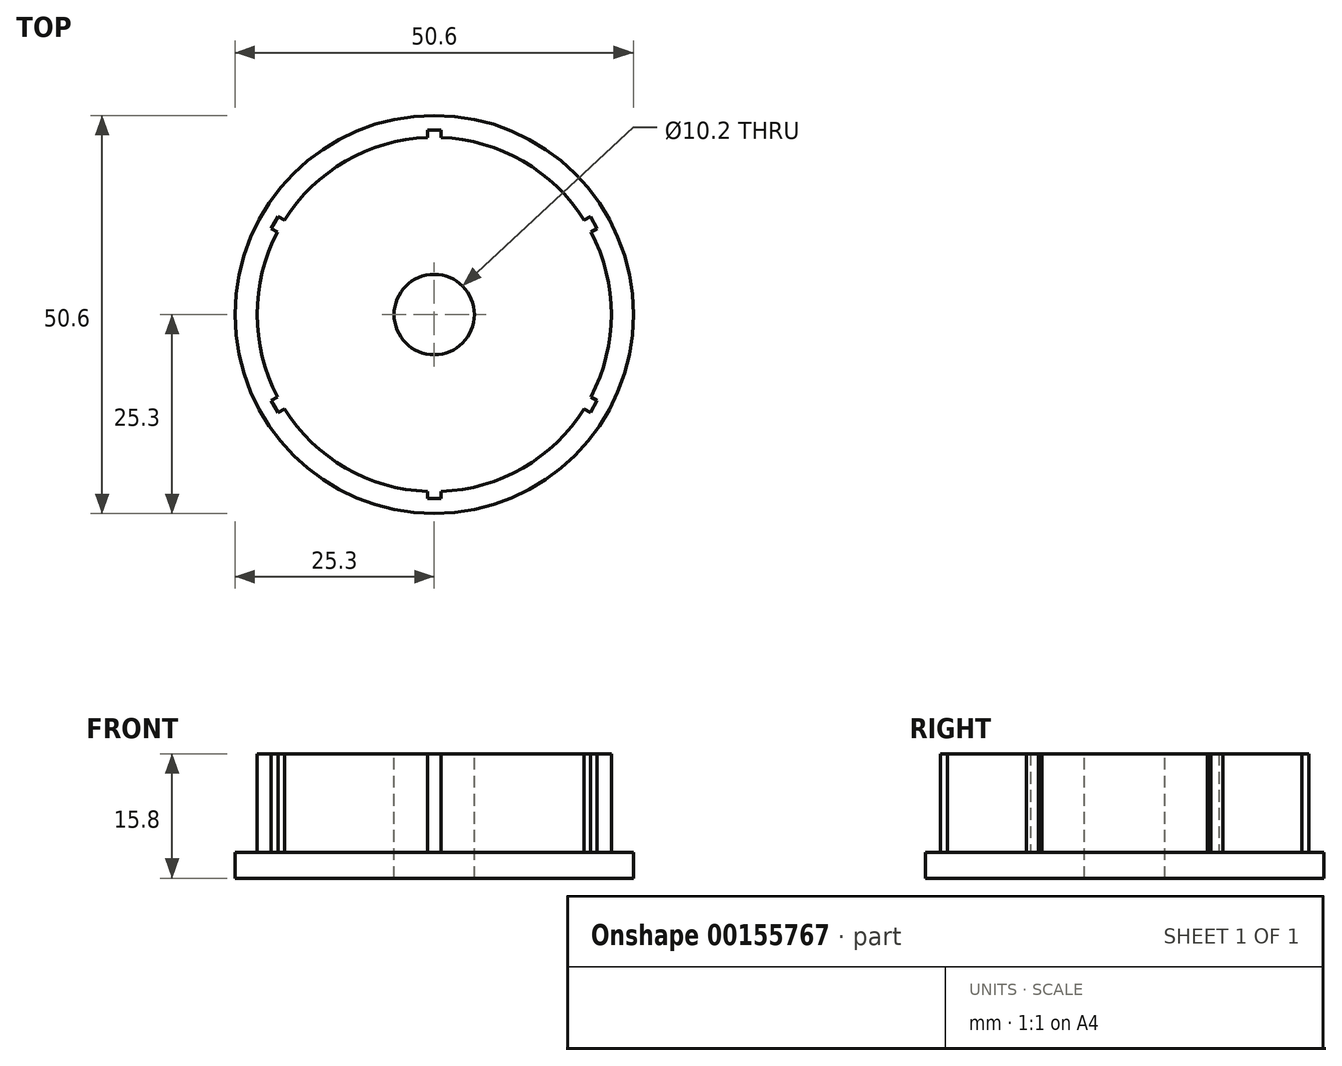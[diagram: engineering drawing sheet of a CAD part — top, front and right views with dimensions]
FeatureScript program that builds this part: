
annotation { "Feature Type Name" : "Feature", "Feature Type Description" : "" }
export const myFeature = defineFeature(function(context is Context, id is Id, definition is map)
    precondition{}
    {
        {
            var Q0;
            Q0=qCreatedBy(makeId("Top.planeOp"),FACE);
            var sketch = newSketch(context, id + "F0", { "sketchPlane" : qUnion([Q0])});
            skCircle(sketch, "E0", {"center": v(0, 0) * mm, "radius": 25.3 * mm});
            skSolve(sketch);
        }
        {
            var Q0;
            Q0 = qSketchRegion(id + "F0", true);
            extrude(context, id + "F1", {"entities" : qUnion([Q0]), "depth" : 3.3 * mm, "offsetDistance" : 25 * mm});
        }
        {
            var Q0;
            Q0=makeQuery(id+"F1.opExtrude","CAP_FACE",FACE,{"disambiguationData":[OSD([sQuery(id+"F0.wireOp",EDGE,"E0")])],"isStart":false});
            var sketch = newSketch(context, id + "F2", { "sketchPlane" : qUnion([Q0])});
            skCircle(sketch, "E1", {"center": v(0, 0) * mm, "radius": 22.5 * mm});
            skLineSegment(sketch, "E2", {"start": v(-0.87, 22.48) * mm, "end": v(-0.88, 23.4) * mm});
            skLineSegment(sketch, "E3.MirrorCS", {"start": v(0.88, 22.48) * mm, "end": v(0.88, 23.4) * mm});
            skLineSegment(sketch, "E4", {"start": v(-0.88, 23.4) * mm, "end": v(0.88, 23.4) * mm});
            skLineSegment(sketch, "E5.1.0", {"start": v(-19.9, 10.48) * mm, "end": v(-20.7, 10.94) * mm});
            skLineSegment(sketch, "E5.1.1", {"start": v(-20.7, 10.94) * mm, "end": v(-19.83, 12.46) * mm});
            skLineSegment(sketch, "E5.1.2", {"start": v(-19.03, 12) * mm, "end": v(-19.83, 12.46) * mm});
            skLineSegment(sketch, "E5.2.0", {"start": v(-19.03, -12) * mm, "end": v(-19.83, -12.46) * mm});
            skLineSegment(sketch, "E5.2.1", {"start": v(-19.83, -12.46) * mm, "end": v(-20.7, -10.94) * mm});
            skLineSegment(sketch, "E5.2.2", {"start": v(-19.9, -10.48) * mm, "end": v(-20.7, -10.94) * mm});
            skLineSegment(sketch, "E5.3.0", {"start": v(0.87, -22.48) * mm, "end": v(0.87, -23.4) * mm});
            skLineSegment(sketch, "E5.3.1", {"start": v(0.87, -23.4) * mm, "end": v(-0.88, -23.4) * mm});
            skLineSegment(sketch, "E5.3.2", {"start": v(-0.88, -22.48) * mm, "end": v(-0.88, -23.4) * mm});
            skLineSegment(sketch, "E5.4.0", {"start": v(19.9, -10.48) * mm, "end": v(20.7, -10.94) * mm});
            skLineSegment(sketch, "E5.4.1", {"start": v(20.7, -10.94) * mm, "end": v(19.83, -12.46) * mm});
            skLineSegment(sketch, "E5.4.2", {"start": v(19.03, -12) * mm, "end": v(19.83, -12.46) * mm});
            skLineSegment(sketch, "E5.5.0", {"start": v(19.03, 12) * mm, "end": v(19.83, 12.46) * mm});
            skLineSegment(sketch, "E5.5.1", {"start": v(19.83, 12.46) * mm, "end": v(20.7, 10.94) * mm});
            skLineSegment(sketch, "E5.5.2", {"start": v(19.9, 10.48) * mm, "end": v(20.7, 10.94) * mm});
            skSolve(sketch);
        }
        {
            var Q0;
            Q0 = qSketchRegion(id + "F2", true);
            extrude(context, id + "F3", {"entities" : qUnion([Q0]), "operationType" : NewBodyOperationType.ADD, "depth" : (15.8 - 3.3) * mm, "offsetDistance" : 25 * mm});
        }
        {
            var Q0;
            Q0=makeQuery(id+"F3.opExtrude","CAP_FACE",FACE,{"disambiguationData":[OSD([sQuery(id+"F2.wireOp",EDGE,"E1"),sQuery(id+"F2.wireOp",EDGE,"E2"),sQuery(id+"F2.wireOp",EDGE,"E3.MirrorCS"),sQuery(id+"F2.wireOp",EDGE,"E4"),sQuery(id+"F2.wireOp",EDGE,"E5.1.0"),sQuery(id+"F2.wireOp",EDGE,"E5.1.1"),sQuery(id+"F2.wireOp",EDGE,"E5.1.2"),sQuery(id+"F2.wireOp",EDGE,"E5.2.0"),sQuery(id+"F2.wireOp",EDGE,"E5.2.1"),sQuery(id+"F2.wireOp",EDGE,"E5.2.2"),sQuery(id+"F2.wireOp",EDGE,"E5.3.0"),sQuery(id+"F2.wireOp",EDGE,"E5.3.1"),sQuery(id+"F2.wireOp",EDGE,"E5.3.2"),sQuery(id+"F2.wireOp",EDGE,"E5.4.0"),sQuery(id+"F2.wireOp",EDGE,"E5.4.1"),sQuery(id+"F2.wireOp",EDGE,"E5.4.2"),sQuery(id+"F2.wireOp",EDGE,"E5.5.0"),sQuery(id+"F2.wireOp",EDGE,"E5.5.1"),sQuery(id+"F2.wireOp",EDGE,"E5.5.2")])],"isStart":false});
            var sketch = newSketch(context, id + "F4", { "sketchPlane" : qUnion([Q0])});
            skCircle(sketch, "E6", {"center": v(0, 0) * mm, "radius": 5.1 * mm});
            skSolve(sketch);
        }
        {
            var Q0;
            Q0 = qSketchRegion(id + "F4", true);
            extrude(context, id + "F5", {"entities" : qUnion([Q0]), "operationType" : NewBodyOperationType.REMOVE, "endBound" : BoundingType.THROUGH_ALL, "oppositeDirection" : true, "depth" : 25 * mm, "offsetDistance" : 25 * mm});
        }
    });
